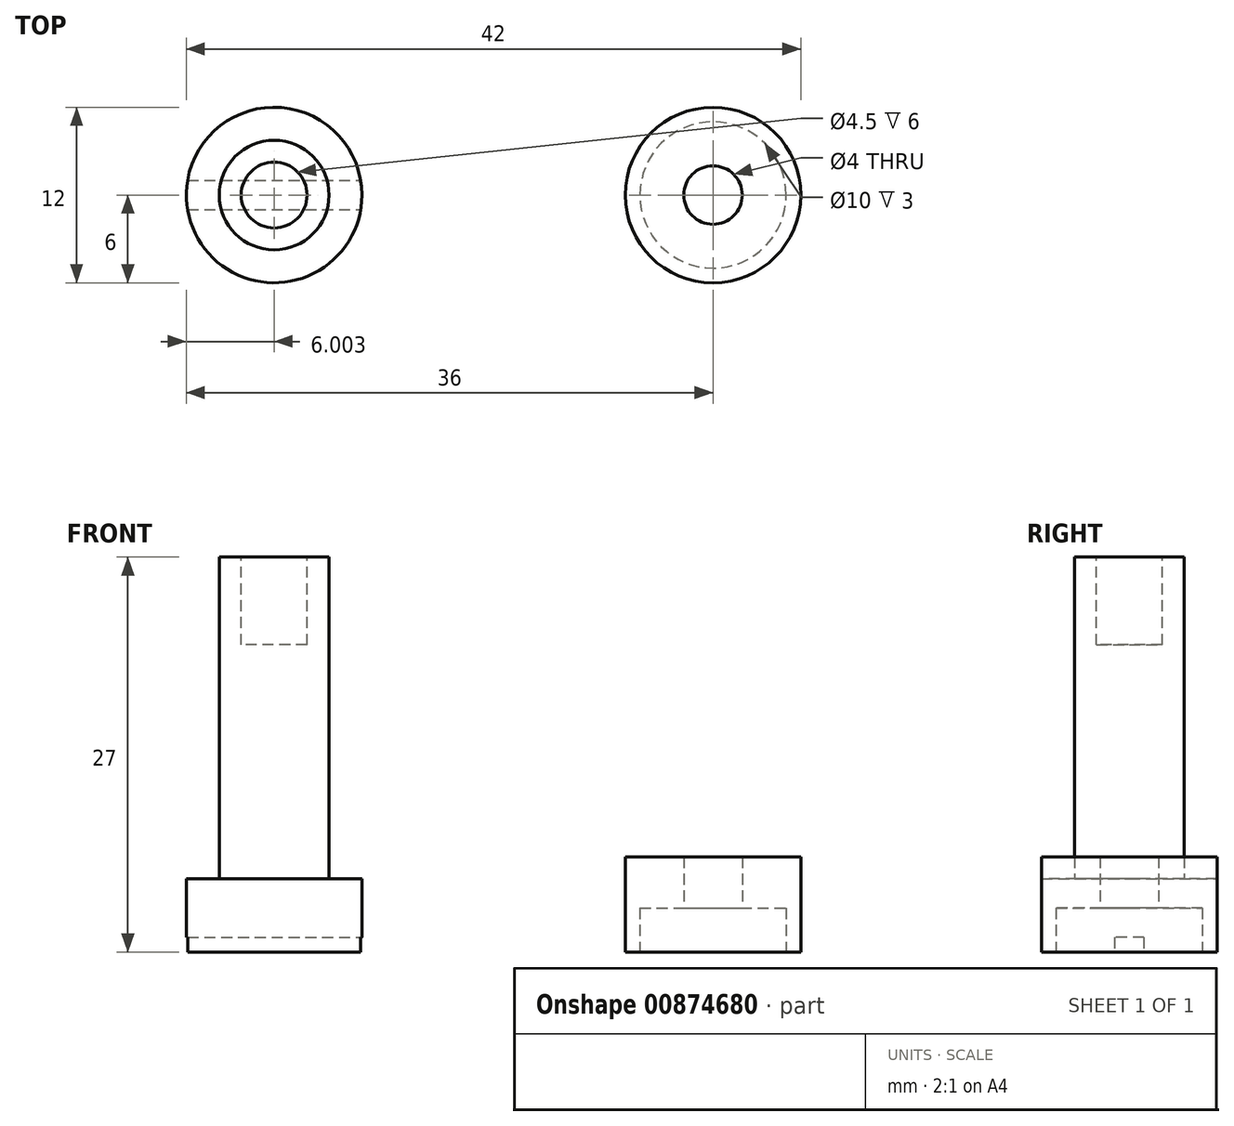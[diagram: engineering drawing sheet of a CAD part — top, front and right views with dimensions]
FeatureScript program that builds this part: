
annotation { "Feature Type Name" : "Feature", "Feature Type Description" : "" }
export const myFeature = defineFeature(function(context is Context, id is Id, definition is map)
    precondition{}
    {
        {
            var Q0;
            Q0=qCreatedBy(makeId("Top.planeOp"),FACE);
            var sketch = newSketch(context, id + "F0", { "sketchPlane" : qUnion([Q0])});
            skCircle(sketch, "E0", {"center": v(0, 0) * mm, "radius": 6 * mm});
            skSolve(sketch);
        }
        {
            var Q0;
            Q0=makeQuery(id+"F0.imprint","IMPRINT",FACE,{"disambiguationData":[TD([[makeQuery(id+"F0.imprint","IMPRINT",EDGE,{"derivedFrom":sQuery(id+"F0.wireOp",EDGE,"E0")}),1.0]])]});
            extrude(context, id + "F1", {"entities" : qUnion([Q0]), "depth" : 6.5 * mm, "offsetDistance" : 25 * mm});
        }
        {
            var Q0;
            Q0=qCreatedBy(makeId("Top.planeOp"),FACE);
            var sketch = newSketch(context, id + "F2", { "sketchPlane" : qUnion([Q0])});
            skCircle(sketch, "E1", {"center": v(-30, 0) * mm, "radius": 6 * mm});
            skSolve(sketch);
        }
        {
            var Q0;
            Q0=makeQuery(id+"F2.imprint","IMPRINT",FACE,{"disambiguationData":[TD([[makeQuery(id+"F2.imprint","IMPRINT",EDGE,{"derivedFrom":sQuery(id+"F2.wireOp",EDGE,"E1")}),1.0]])]});
            extrude(context, id + "F3", {"entities" : qUnion([Q0]), "depth" : 5 * mm, "offsetDistance" : 25 * mm});
        }
        {
            var Q0;
            Q0=makeQuery(id+"F3.opExtrude","CAP_FACE",FACE,{"disambiguationData":[OSD([sQuery(id+"F2.wireOp",EDGE,"E1")])],"isStart":false});
            var sketch = newSketch(context, id + "F4", { "sketchPlane" : qUnion([Q0])});
            skCircle(sketch, "E2", {"center": v(-30, 0) * mm, "radius": 3.75 * mm});
            skSolve(sketch);
        }
        {
            var Q0;
            Q0=makeQuery(id+"F4.imprint","IMPRINT",FACE,{"disambiguationData":[TD([[makeQuery(id+"F4.imprint","IMPRINT",EDGE,{"derivedFrom":sQuery(id+"F4.wireOp",EDGE,"E2")}),1.0]])]});
            extrude(context, id + "F5", {"entities" : qUnion([Q0]), "operationType" : NewBodyOperationType.ADD, "depth" : 22 * mm, "offsetDistance" : 25 * mm});
        }
        {
            var Q0;
            Q0=makeQuery(id+"F3.opExtrude","CAP_FACE",FACE,{"disambiguationData":[OSD([sQuery(id+"F2.wireOp",EDGE,"E1")])],"isStart":true});
            var sketch = newSketch(context, id + "F6", { "sketchPlane" : qUnion([Q0])});
            skLineSegment(sketch, "E3.bottom", {"start": v(-35.91, 1) * mm, "end": v(-24.08, 1) * mm});
            skLineSegment(sketch, "E3.top", {"start": v(-35.91, -1) * mm, "end": v(-24.08, -1) * mm});
            skLineSegment(sketch, "E3.left", {"start": v(-35.91, 1) * mm, "end": v(-35.91, -1) * mm});
            skLineSegment(sketch, "E3.right", {"start": v(-24.08, 1) * mm, "end": v(-24.08, -1) * mm});
            skSolve(sketch);
        }
        {
            var Q0;
            {var subQ0=sQuery(id+"F6.wireOp",EDGE,"E3.left");Q0=makeQuery(id+"F6.imprint","IMPRINT",FACE,{"disambiguationData":[TD([[makeQuery(id+"F6.imprint","IMPRINT",EDGE,{"derivedFrom":subQ0}),-1.0]])]});}
            var Q1;
            Q1=makeQuery(id+"F6.imprint","IMPRINT",FACE,{"disambiguationData":[TD([[makeQuery(id+"F6.imprint","IMPRINT",EDGE,{"derivedFrom":sQuery(id+"F6.wireOp",EDGE,"E3.bottom")}),-1.0]])]});
            var Q2;
            {var subQ0=sQuery(id+"F6.wireOp",EDGE,"E3.right");Q2=makeQuery(id+"F6.imprint","IMPRINT",FACE,{"disambiguationData":[TD([[makeQuery(id+"F6.imprint","IMPRINT",EDGE,{"derivedFrom":subQ0}),1.0]])]});}
            extrude(context, id + "F7", {"entities" : qUnion([Q0, Q1, Q2]), "operationType" : NewBodyOperationType.REMOVE, "oppositeDirection" : true, "depth" : 1 * mm, "offsetDistance" : 25 * mm});
        }
        {
            var Q0;
            Q0=makeQuery(id+"F5.opExtrude","CAP_FACE",FACE,{"disambiguationData":[OSD([sQuery(id+"F4.wireOp",EDGE,"E2")])],"isStart":false});
            var sketch = newSketch(context, id + "F8", { "sketchPlane" : qUnion([Q0])});
            skSolve(sketch);
        }
        {
            var Q0;
            Q0=makeQuery(id+"F1.opExtrude","CAP_FACE",FACE,{"disambiguationData":[OSD([sQuery(id+"F0.wireOp",EDGE,"E0")])],"isStart":true});
            var sketch = newSketch(context, id + "F9", { "sketchPlane" : qUnion([Q0])});
            skPoint(sketch, "E4", {"position": v(0, 0) * mm});
            skSolve(sketch);
        }
        {
            var Q0;
            Q0=sQuery(id+"F9.wireOp",VERTEX,"E4");
            var Q1;
            Q1=makeQuery(id+"F1.opExtrude","SWEPT_BODY",BODY,{"disambiguationData":[OSD([sQuery(id+"F0.wireOp",EDGE,"E0")])]});
            hole(context, id + "F10", {"style" : HoleStyle.C_BORE, "endStyle" : HoleEndStyle.THROUGH, "holeDiameter" : 4 * mm, "cBoreDiameter" : 10 * mm, "cBoreDepth" : 3 * mm, "majorDiameter" : 5 * mm, "isTappedThrough" : true, "tappedDepth" : 12 * mm, "tapClearance" : 3, "startFromSketch" : true, "locations" : qUnion([Q0]), "scope" : qUnion([Q1])});
        }
        {
            var Q0;
            Q0=makeQuery(id+"F8.imprint","IMPRINT",FACE,{"disambiguationData":[TD([[makeQuery(id+"F8.imprint","IMPRINT",EDGE,{"derivedFrom":makeQuery(id+"F5.opExtrude","CAP_EDGE",EDGE,{"disambiguationData":[OSD([sQuery(id+"F4.wireOp",EDGE,"E2")])],"isStart":false})}),1.0]])]});
            var sketch = newSketch(context, id + "F11", { "sketchPlane" : qUnion([Q0])});
            skCircle(sketch, "E5", {"center": v(-30, 0) * mm, "radius": 2.25 * mm});
            skSolve(sketch);
        }
        {
            var Q0;
            Q0 = qSketchRegion(id + "F11", true);
            extrude(context, id + "F12", {"entities" : qUnion([Q0]), "operationType" : NewBodyOperationType.REMOVE, "oppositeDirection" : true, "depth" : 6 * mm, "offsetDistance" : 25 * mm});
        }
    });
